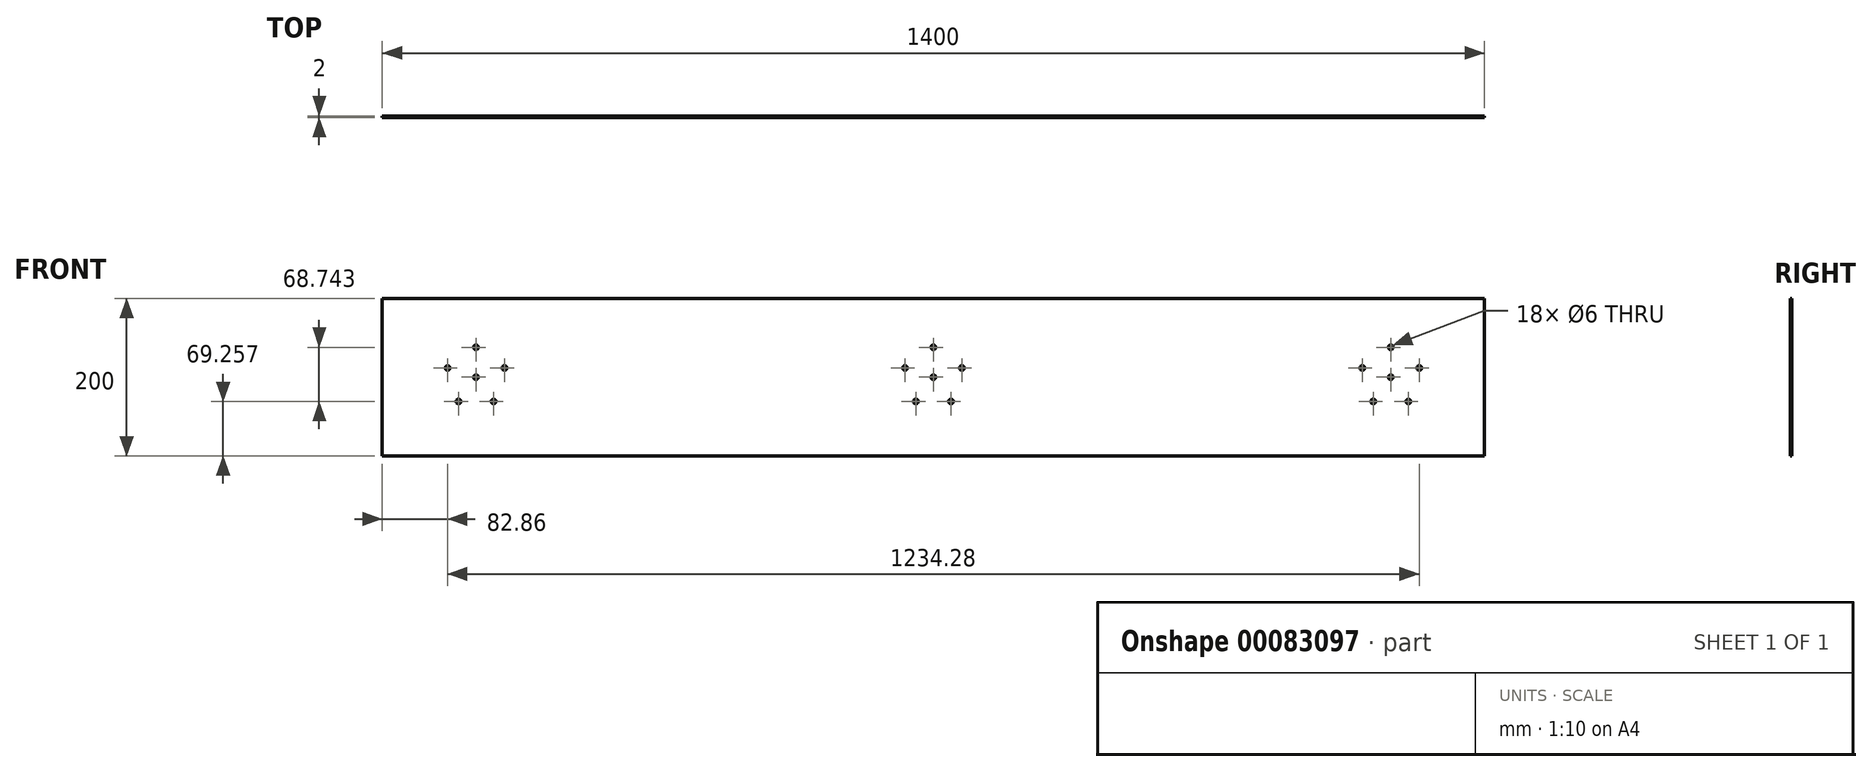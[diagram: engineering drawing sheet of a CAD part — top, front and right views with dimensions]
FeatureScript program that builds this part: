
annotation { "Feature Type Name" : "Feature", "Feature Type Description" : "" }
export const myFeature = defineFeature(function(context is Context, id is Id, definition is map)
    precondition{}
    {
        {
            var Q0;
            Q0=qCreatedBy(makeId("Front.planeOp"),FACE);
            var sketch = newSketch(context, id + "F0", { "sketchPlane" : qUnion([Q0])});
            skLineSegment(sketch, "E0.bottom", {"start": v(0, 0) * mm, "end": v(1400, 0) * mm});
            skLineSegment(sketch, "E0.top", {"start": v(0, 200) * mm, "end": v(1400, 200) * mm});
            skLineSegment(sketch, "E0.left", {"start": v(0, 0) * mm, "end": v(0, 200) * mm});
            skLineSegment(sketch, "E0.right", {"start": v(1400, 0) * mm, "end": v(1400, 200) * mm});
            skSolve(sketch);
        }
        {
            var Q0;
            Q0 = qSketchRegion(id + "F0", true);
            extrude(context, id + "F1", {"entities" : qUnion([Q0]), "depth" : 2 * mm});
        }
        {
            var Q0;
            Q0=makeQuery(id+"F1.opExtrude","CAP_FACE",FACE,{"disambiguationData":[OSD([sQuery(id+"F0.wireOp",EDGE,"E0.bottom"),sQuery(id+"F0.wireOp",EDGE,"E0.top"),sQuery(id+"F0.wireOp",EDGE,"E0.left"),sQuery(id+"F0.wireOp",EDGE,"E0.right")])],"isStart":false});
            var sketch = newSketch(context, id + "F2", { "sketchPlane" : qUnion([Q0])});
            skCircle(sketch, "E1", {"center": v(700, 100) * mm, "radius": 3 * mm});
            skCircle(sketch, "E2", {"center": v(700, 138) * mm, "radius": 3 * mm});
            skCircle(sketch, "E3.1.0", {"center": v(663.86, 111.74) * mm, "radius": 3 * mm});
            skCircle(sketch, "E3.2.0", {"center": v(677.66, 69.26) * mm, "radius": 3 * mm});
            skCircle(sketch, "E3.3.0", {"center": v(722.34, 69.26) * mm, "radius": 3 * mm});
            skCircle(sketch, "E3.4.0", {"center": v(736.14, 111.74) * mm, "radius": 3 * mm});
            skLineSegment(sketch, "E4", {"start": v(409.5, 213.26) * mm, "end": v(409.5, -23.06) * mm});
            skCircle(sketch, "E5.MirrorC", {"center": v(119, 138) * mm, "radius": 3 * mm});
            skCircle(sketch, "E6.MirrorC", {"center": v(82.86, 111.74) * mm, "radius": 3 * mm});
            skCircle(sketch, "E7.MirrorC", {"center": v(96.66, 69.26) * mm, "radius": 3 * mm});
            skCircle(sketch, "E8.MirrorC", {"center": v(155.14, 111.74) * mm, "radius": 3 * mm});
            skCircle(sketch, "E9.MirrorC", {"center": v(119, 100) * mm, "radius": 3 * mm});
            skLineSegment(sketch, "E10", {"start": v(990.5, 264.57) * mm, "end": v(990.5, -126.3) * mm});
            skCircle(sketch, "E11.MirrorC", {"center": v(141.34, 69.26) * mm, "radius": 3 * mm});
            skCircle(sketch, "E12.MirrorC", {"center": v(1317.14, 111.74) * mm, "radius": 3 * mm});
            skCircle(sketch, "E13.MirrorC", {"center": v(1303.34, 69.26) * mm, "radius": 3 * mm});
            skCircle(sketch, "E14.MirrorC", {"center": v(1258.66, 69.26) * mm, "radius": 3 * mm});
            skCircle(sketch, "E15.MirrorC", {"center": v(1244.86, 111.74) * mm, "radius": 3 * mm});
            skCircle(sketch, "E16.MirrorC", {"center": v(1281, 100) * mm, "radius": 3 * mm});
            skCircle(sketch, "E17.MirrorC", {"center": v(1281, 138) * mm, "radius": 3 * mm});
            skSolve(sketch);
        }
        {
            var Q0;
            Q0 = qSketchRegion(id + "F2", true);
            extrude(context, id + "F3", {"entities" : qUnion([Q0]), "operationType" : NewBodyOperationType.REMOVE, "endBound" : BoundingType.THROUGH_ALL, "oppositeDirection" : true, "depth" : 25 * mm});
        }
    });
